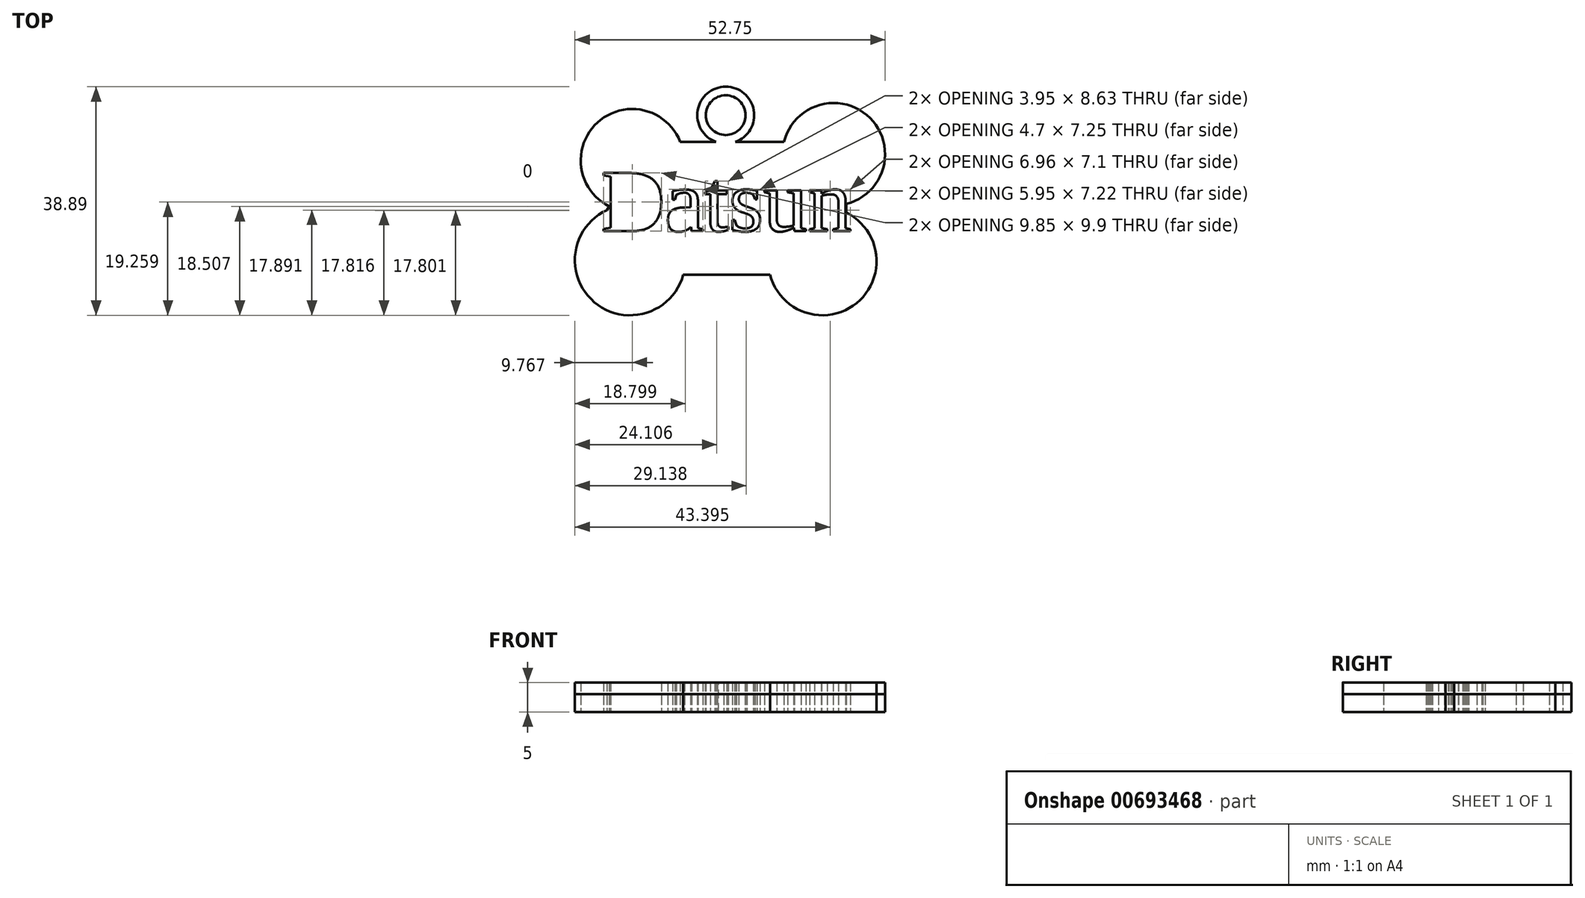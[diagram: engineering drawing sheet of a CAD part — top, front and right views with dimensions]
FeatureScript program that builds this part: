
annotation { "Feature Type Name" : "Feature", "Feature Type Description" : "" }
export const myFeature = defineFeature(function(context is Context, id is Id, definition is map)
    precondition{}
    {
        {
            var Q0;
            Q0=qCreatedBy(makeId("Top.planeOp"),FACE);
            var sketch = newSketch(context, id + "F0", { "sketchPlane" : qUnion([Q0])});
            skLineSegment(sketch, "E0", {"start": v(40.2, 51.36) * mm, "end": v(46.6, 51.36) * mm});
            skLineSegment(sketch, "E1", {"start": v(40.72, 28.79) * mm, "end": v(55.07, 28.79) * mm});
            skArc(sketch, "E2", {"start": v(28.06, 39.76) * mm, "mid": v(25.9, 24.08) * mm, "end": v(41.02, 28.79) * mm});
            skArc(sketch, "E3", {"start": v(68.72, 40.8) * mm, "mid": v(72.78, 55.43) * mm, "end": v(58.15, 51.36) * mm});
            skArc(sketch, "E4", {"start": v(55.78, 28.79) * mm, "mid": v(70.5, 23.93) * mm, "end": v(68.72, 39.34) * mm});
            skLineSegment(sketch, "E5", {"start": v(68.72, 40.8) * mm, "end": v(68.72, 39.34) * mm});
            skLineSegment(sketch, "E6", {"start": v(57.17, 51.36) * mm, "end": v(58.15, 51.36) * mm});
            skLineSegment(sketch, "E7", {"start": v(55.78, 28.79) * mm, "end": v(55.07, 28.79) * mm});
            skArc(sketch, "E8", {"start": v(49.9, 51.36) * mm, "mid": v(48.24, 60.75) * mm, "end": v(46.6, 51.36) * mm});
            skCircle(sketch, "E9", {"center": v(48.24, 55.91) * mm, "radius": 3.38 * mm});
            skText(sketch, "E10", { "text": "Datsun", "fontName": "Tinos-Regular.ttf"});
            skArc(sketch, "E11", {"start": v(40.5, 51.36) * mm, "mid": v(26.44, 54.69) * mm, "end": v(28.44, 40.39) * mm});
            skLineSegment(sketch, "E12", {"start": v(40.46, 51.43) * mm, "end": v(43.56, 51.36) * mm});
            skLineSegment(sketch, "E13", {"start": v(28.44, 40.39) * mm, "end": v(28.06, 39.76) * mm});
            skLineSegment(sketch, "E14.trimOffspring", {"start": v(49.9, 51.36) * mm, "end": v(57.17, 51.36) * mm});
            const initialGuessF0  = {"E10": [0.027, 0.0362, 1, 0, 0.01085]};
            skSetInitialGuess(sketch, initialGuessF0);
            skSolve(sketch);
        }
        {
            var Q0;
            {var subQ6=sQuery(id+"F0.wireOp",EDGE,"E2");Q0=makeQuery(id+"F0.imprint","IMPRINT",FACE,{"disambiguationData":[TD([[makeQuery(id+"F0.imprint","IMPRINT",EDGE,{"derivedFrom":subQ6}),1.0]])]});}
            extrude(context, id + "F1", {"entities" : qUnion([Q0]), "depth" : 5 * mm, "offsetDistance" : 25 * mm});
        }
        {
            var Q0;
            Q0=makeQuery(id+"F0.imprint","IMPRINT",FACE,{"disambiguationData":[TD([[makeQuery(id+"F0.imprint","IMPRINT",EDGE,{"derivedFrom":sQuery(id+"F0.wireOp",EDGE,"E9")}),-1.0]])]});
            extrude(context, id + "F2", {"entities" : qUnion([Q0]), "depth" : 3 * mm, "offsetDistance" : 25 * mm});
        }
    });
